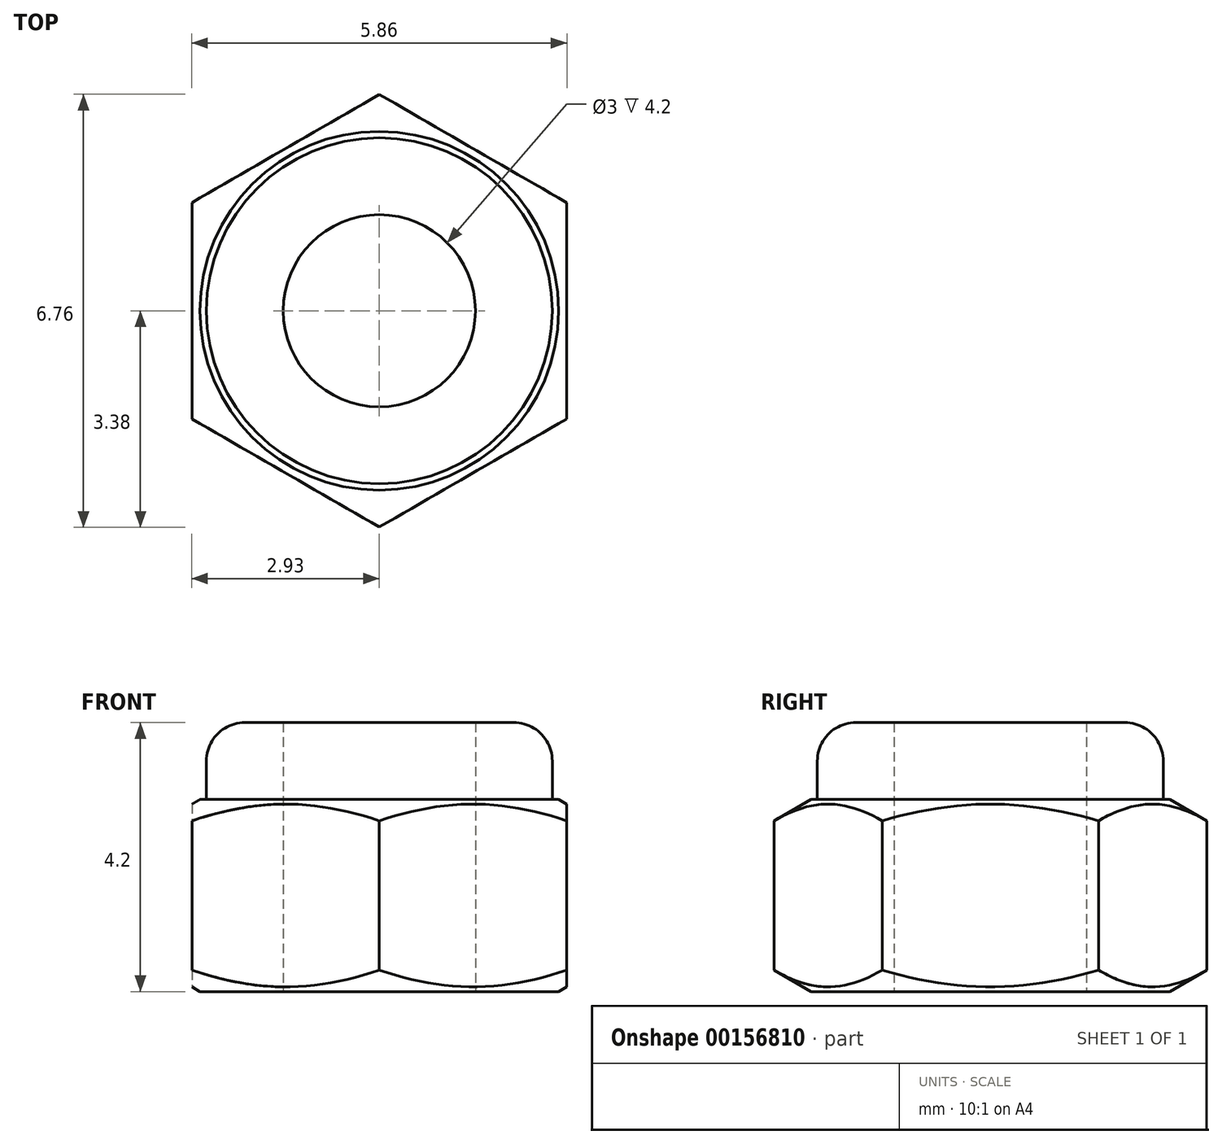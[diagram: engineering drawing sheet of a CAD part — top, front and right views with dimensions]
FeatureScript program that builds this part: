
annotation { "Feature Type Name" : "Feature", "Feature Type Description" : "" }
export const myFeature = defineFeature(function(context is Context, id is Id, definition is map)
    precondition{}
    {
        {
            var Q0;
            Q0=qCreatedBy(makeId("Top.planeOp"),FACE);
            var sketch = newSketch(context, id + "F0", { "sketchPlane" : qUnion([Q0])});
            skCircle(sketch, "E0.cCircle", {"center": v(0, 0) * mm, "radius": 2.93 * mm, "construction": true});
            skLineSegment(sketch, "E0.0", {"start": v(2.93, 1.69) * mm, "end": v(2.93, -1.69) * mm});
            skLineSegment(sketch, "E0.1", {"start": v(2.92, -1.69) * mm, "end": v(0, -3.38) * mm});
            skLineSegment(sketch, "E0.2", {"start": v(0, -3.38) * mm, "end": v(-2.92, -1.69) * mm});
            skLineSegment(sketch, "E0.3", {"start": v(-2.93, -1.69) * mm, "end": v(-2.93, 1.69) * mm});
            skLineSegment(sketch, "E0.4", {"start": v(-2.93, 1.69) * mm, "end": v(0, 3.38) * mm});
            skLineSegment(sketch, "E0.5", {"start": v(0, 3.38) * mm, "end": v(2.92, 1.69) * mm});
            skPoint(sketch, "E0.0.midPoint", {"position": v(2.93, 0) * mm});
            skCircle(sketch, "E1", {"center": v(0, 0) * mm, "radius": 1.5 * mm});
            skSolve(sketch);
        }
        {
            var Q0;
            Q0=qSketchRegion(id+"F0",true);
            extrude(context, id + "F1", {"entities" : qUnion([Q0]), "depth" : 3 * mm});
        }
        {
            var Q0;
            Q0=qCreatedBy(makeId("Front.planeOp"),FACE);
            var sketch = newSketch(context, id + "F2", { "sketchPlane" : qUnion([Q0])});
            skLineSegment(sketch, "E2", {"start": v(0, 0) * mm, "end": v(0, 3) * mm, "construction": true});
            skLineSegment(sketch, "E3", {"start": v(0, 1.5) * mm, "end": v(2.92, 1.5) * mm, "construction": true});
            skPoint(sketch, "E3.endSnap0", {"position": v(0, 1.5) * mm});
            skLineSegment(sketch, "E4", {"start": v(2.8, 3) * mm, "end": v(4.88, 3) * mm});
            skLineSegment(sketch, "E5", {"start": v(4.88, 3) * mm, "end": v(4.88, 1.8) * mm});
            skLineSegment(sketch, "E6", {"start": v(4.88, 1.8) * mm, "end": v(2.8, 3) * mm});
            skLineSegment(sketch, "E7.MirrorCS", {"start": v(4.88, 0) * mm, "end": v(4.88, 1.2) * mm});
            skLineSegment(sketch, "E8.MirrorCS", {"start": v(2.8, 0) * mm, "end": v(4.88, 0) * mm});
            skLineSegment(sketch, "E9.MirrorCS", {"start": v(4.88, 1.2) * mm, "end": v(2.8, 0) * mm});
            skSolve(sketch);
        }
        {
            var Q0;
            Q0=qSketchRegion(id+"F2",true);
            var Q1;
            Q1=sQuery(id+"F2.wireOp",EDGE,"E2");
            revolve(context, id + "F3", {"operationType" : NewBodyOperationType.REMOVE, "entities" : qUnion([Q0]), "axis" : qUnion([Q1]), "revolveType" : RevolveType.FULL});
        }
        {
            var Q0;
            Q0=qCreatedBy(makeId("Front.planeOp"),FACE);
            var sketch = newSketch(context, id + "F4", { "sketchPlane" : qUnion([Q0])});
            skLineSegment(sketch, "E10", {"start": v(1.5, 3) * mm, "end": v(2.7, 3) * mm});
            skLineSegment(sketch, "E11", {"start": v(2.7, 3) * mm, "end": v(2.7, 4.2) * mm});
            skLineSegment(sketch, "E12", {"start": v(2.7, 4.2) * mm, "end": v(1.5, 4.2) * mm});
            skLineSegment(sketch, "E13", {"start": v(1.5, 4.2) * mm, "end": v(1.5, 3) * mm});
            skSolve(sketch);
        }
        {
            var Q0;
            Q0=qSketchRegion(id+"F4",true);
            var Q1;
            Q1=sQuery(id+"F2.wireOp",EDGE,"E2");
            revolve(context, id + "F5", {"operationType" : NewBodyOperationType.ADD, "entities" : qUnion([Q0]), "axis" : qUnion([Q1]), "revolveType" : RevolveType.FULL});
        }
        {
            var Q0;
            Q0=makeQuery(id+"F5.opRevolve","SWEPT_EDGE",EDGE,{"disambiguationData":[OSD([sQuery(id+"F4.wireOp",EDGE,"E11"),sQuery(id+"F4.wireOp",EDGE,"E12")])]});
            fillet(context, id + "F6", {"entities" : qUnion([Q0]), "radius" : .6 * mm, "tangentPropagation" : true, "allowEdgeOverflow" : false});
        }
    });
